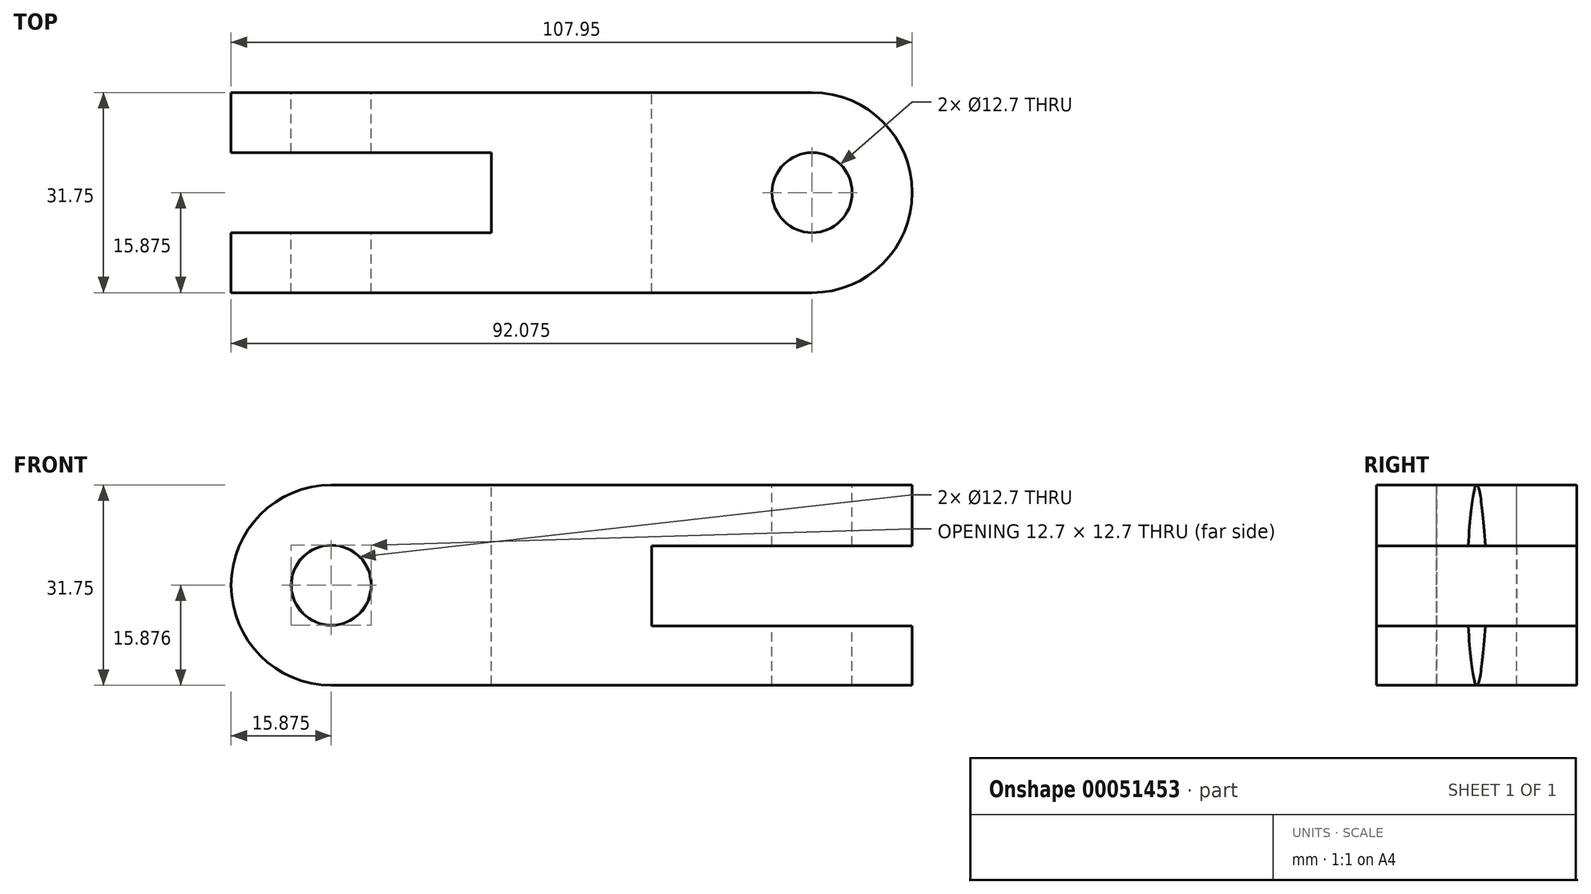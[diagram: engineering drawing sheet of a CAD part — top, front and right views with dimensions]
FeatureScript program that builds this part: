
annotation { "Feature Type Name" : "Feature", "Feature Type Description" : "" }
export const myFeature = defineFeature(function(context is Context, id is Id, definition is map)
    precondition{}
    {
        {
            var Q0;
            Q0=qCreatedBy(makeId("Front.planeOp"),FACE);
            var sketch = newSketch(context, id + "F0", { "sketchPlane" : qUnion([Q0])});
            skLineSegment(sketch, "E0.bottom", {"start": v(-38.35, 11.35) * mm, "end": v(53.73, 11.35) * mm});
            skLineSegment(sketch, "E0.top", {"start": v(-38.35, -20.4) * mm, "end": v(53.73, -20.4) * mm});
            skCircle(sketch, "E1", {"center": v(-38.35, -4.52) * mm, "radius": 6.35 * mm});
            skLineSegment(sketch, "E2.0", {"start": v(-38.35, -4.52) * mm, "end": v(-38.35, -4.52) * mm});
            skLineSegment(sketch, "E2.1", {"start": v(-38.35, -4.52) * mm, "end": v(-32, -4.52) * mm, "construction": true});
            skLineSegment(sketch, "E2.2", {"start": v(0.46, -4.52) * mm, "end": v(0.46, -4.52) * mm});
            skLineSegment(sketch, "E2.3", {"start": v(-38.35, -4.52) * mm, "end": v(-32, -4.52) * mm, "construction": true});
            skArc(sketch, "E3", {"start": v(-38.35, 11.35) * mm, "mid": v(-54.22, -4.52) * mm, "end": v(-38.35, -20.4) * mm});
            skLineSegment(sketch, "E4", {"start": v(-38.35, -4.52) * mm, "end": v(-54.22, -4.52) * mm, "construction": true});
            skLineSegment(sketch, "E5.bottom", {"start": v(12.4, 1.7) * mm, "end": v(53.67, 1.7) * mm});
            skLineSegment(sketch, "E5.top", {"start": v(12.4, -11) * mm, "end": v(53.67, -11) * mm});
            skLineSegment(sketch, "E5.left", {"start": v(12.4, 1.7) * mm, "end": v(12.4, -11) * mm});
            skLineSegment(sketch, "E6", {"start": v(53.73, -4.52) * mm, "end": v(12.4, -4.64) * mm, "construction": true});
            skLineSegment(sketch, "E7", {"start": v(-32, -4.52) * mm, "end": v(12.4, -4.64) * mm, "construction": true});
            skLineSegment(sketch, "E8", {"start": v(53.73, 11.35) * mm, "end": v(53.67, 1.7) * mm});
            skLineSegment(sketch, "E9", {"start": v(53.67, 1.7) * mm, "end": v(53.67, -11) * mm});
            skLineSegment(sketch, "E10", {"start": v(53.67, -11) * mm, "end": v(53.73, -20.4) * mm});
            skSolve(sketch);
        }
        {
            var Q0;
            Q0=makeQuery(id+"F0.imprint","IMPRINT",FACE,{"disambiguationData":[TD([[makeQuery(id+"F0.imprint","IMPRINT",EDGE,{"derivedFrom":sQuery(id+"F0.wireOp",EDGE,"E0.bottom")}),-1.0]])]});
            extrude(context, id + "F1", {"entities" : qUnion([Q0]), "depth" : 31.75 * mm});
        }
        {
            var Q0;
            Q0=makeQuery(id+"F1.opExtrude","SWEPT_FACE",FACE,{"disambiguationData":[OSD([sQuery(id+"F0.wireOp",EDGE,"E0.bottom")])]});
            var sketch = newSketch(context, id + "F2", { "sketchPlane" : qUnion([Q0])});
            skLineSegment(sketch, "E11", {"start": v(37.85, 0) * mm, "end": v(-54.23, 0) * mm});
            skLineSegment(sketch, "E12", {"start": v(-54.23, 0) * mm, "end": v(-54.23, -31.78) * mm});
            skLineSegment(sketch, "E13.0", {"start": v(-54.24, -22.26) * mm, "end": v(-12.96, -22.24) * mm});
            skLineSegment(sketch, "E14.0", {"start": v(-12.96, -9.53) * mm, "end": v(-12.96, -22.24) * mm});
            skCircle(sketch, "E15", {"center": v(37.85, -15.88) * mm, "radius": 6.35 * mm});
            skArc(sketch, "E16", {"start": v(37.85, -31.75) * mm, "mid": v(53.73, -15.88) * mm, "end": v(37.85, 0) * mm});
            skLineSegment(sketch, "E17.trimOffspring", {"start": v(-12.96, -9.53) * mm, "end": v(-54.23, -9.53) * mm});
            skLineSegment(sketch, "E18.trimOffspring", {"start": v(37.85, -22.23) * mm, "end": v(37.85, -22.23) * mm});
            skLineSegment(sketch, "E19", {"start": v(-54.23, -31.78) * mm, "end": v(37.85, -31.75) * mm});
            skSolve(sketch);
        }
        {
            var Q0;
            {var subQ0=sQuery(id+"F2.wireOp",EDGE,"E14.0");Q0=makeQuery(id+"F2.imprint","IMPRINT",FACE,{"disambiguationData":[TD([[makeQuery(id+"F2.imprint","IMPRINT",EDGE,{"derivedFrom":subQ0}),-1.0]])]});}
            var Q1;
            {var subQ0=sQuery(id+"F2.wireOp",EDGE,"E17.trimOffspring");var subQ1=sQuery(id+"F2.wireOp",EDGE,"E12");var subQ2=makeQuery(id+"F2.imprint","INTERSECT",VERTEX,{"derivedFrom":[subQ1,subQ0]});Q1=makeQuery(id+"F2.imprint","IMPRINT",FACE,{"disambiguationData":[TD([[makeQuery(id+"F2.imprint","IMPRINT",EDGE,{"disambiguationData":[TD([[subQ2,-1.0]])],"derivedFrom":subQ1}),1.0]])]});}
            var Q2;
            Q2=makeQuery(id+"F2.imprint","IMPRINT",FACE,{"disambiguationData":[TD([[makeQuery(id+"F2.imprint","IMPRINT",EDGE,{"derivedFrom":sQuery(id+"F2.wireOp",EDGE,"E15")}),1.0]])]});
            var Q3;
            {var subQ0=sQuery(id+"F2.wireOp",EDGE,"E16");var subQ1=sQuery(id+"F0.wireOp",EDGE,"E0.bottom");var subQ2=makeQuery(id+"F1.opExtrude","CAP_EDGE",EDGE,{"disambiguationData":[OSD([subQ1])],"isStart":true});var subQ3=makeQuery(id+"F2.imprint","INTERSECT",VERTEX,{"derivedFrom":[subQ2,sQuery(id+"F2.wireOp",EDGE,"E11"),subQ0]});Q3=makeQuery(id+"F2.imprint","IMPRINT",FACE,{"disambiguationData":[TD([[makeQuery(id+"F2.imprint","IMPRINT",EDGE,{"disambiguationData":[TD([[subQ3,1.0]])],"derivedFrom":subQ0}),-1.0]])]});}
            var Q4;
            {var subQ0=sQuery(id+"F2.wireOp",EDGE,"E16");var subQ1=sQuery(id+"F0.wireOp",EDGE,"E0.bottom");var subQ2=makeQuery(id+"F1.opExtrude","CAP_EDGE",EDGE,{"disambiguationData":[OSD([subQ1])],"isStart":false});var subQ3=makeQuery(id+"F2.imprint","INTERSECT",VERTEX,{"derivedFrom":[subQ2,subQ0,sQuery(id+"F2.wireOp",EDGE,"E19")]});Q4=makeQuery(id+"F2.imprint","IMPRINT",FACE,{"disambiguationData":[TD([[makeQuery(id+"F2.imprint","IMPRINT",EDGE,{"disambiguationData":[TD([[subQ3,-1.0]])],"derivedFrom":subQ0}),-1.0]])]});}
            extrude(context, id + "F3", {"entities" : qUnion([Q0, Q1, Q2, Q3, Q4]), "operationType" : NewBodyOperationType.REMOVE, "endBound" : BoundingType.THROUGH_ALL, "oppositeDirection" : true, "depth" : 25.4 * mm});
        }
    });
